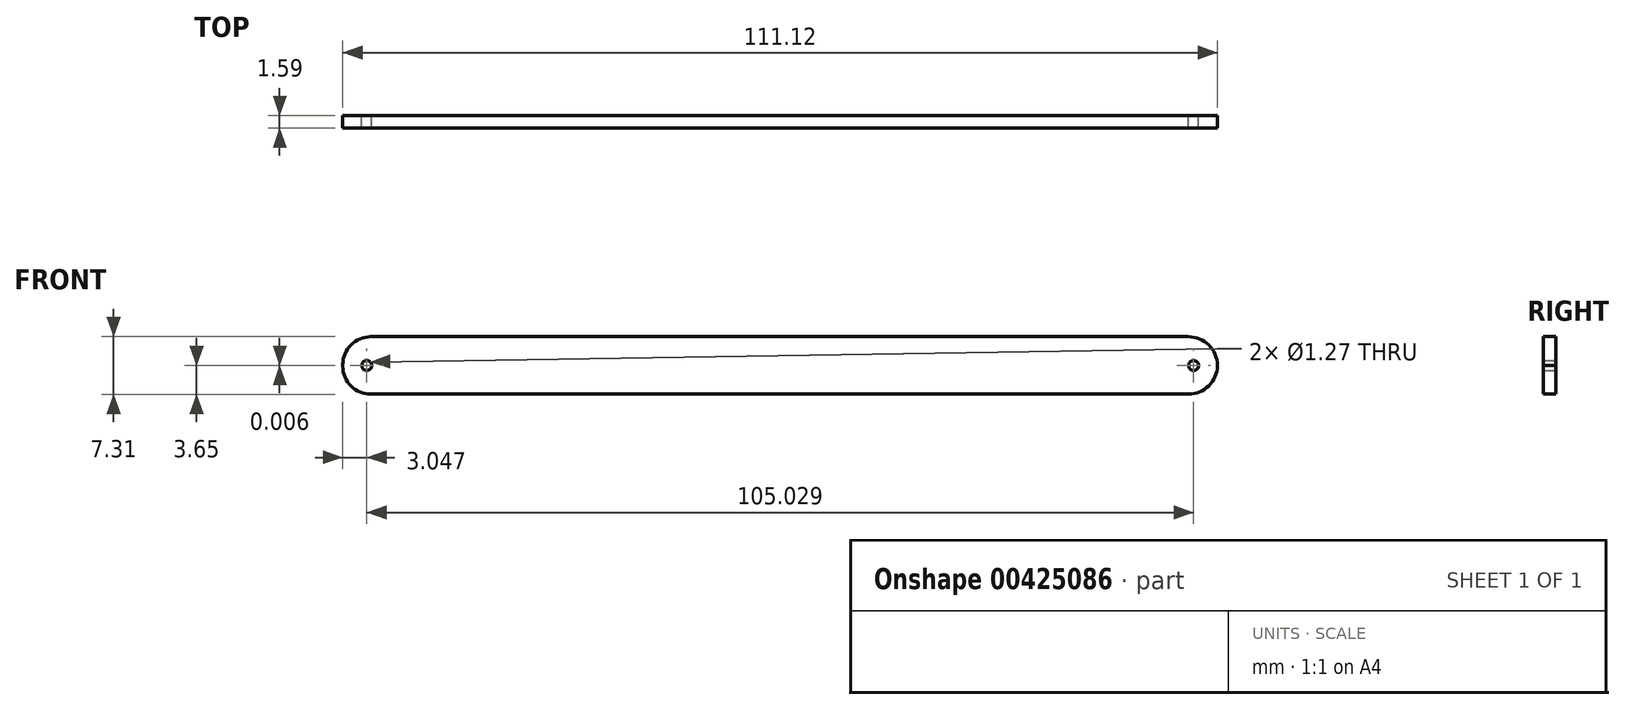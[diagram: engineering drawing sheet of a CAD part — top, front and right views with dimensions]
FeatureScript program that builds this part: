
annotation { "Feature Type Name" : "Feature", "Feature Type Description" : "" }
export const myFeature = defineFeature(function(context is Context, id is Id, definition is map)
    precondition{}
    {
        {
            var Q0;
            Q0=qCreatedBy(makeId("Front.planeOp"),FACE);
            var sketch = newSketch(context, id + "F0", { "sketchPlane" : qUnion([Q0])});
            skLineSegment(sketch, "E0.bottom", {"start": v(-46.8, 13.78) * mm, "end": v(64.33, 13.78) * mm});
            skLineSegment(sketch, "E0.top", {"start": v(-46.8, 6.47) * mm, "end": v(64.33, 6.47) * mm});
            skLineSegment(sketch, "E0.left", {"start": v(-46.8, 13.78) * mm, "end": v(-46.8, 6.47) * mm});
            skLineSegment(sketch, "E0.right", {"start": v(64.33, 13.78) * mm, "end": v(64.33, 6.47) * mm});
            skCircle(sketch, "E1", {"center": v(-43.74, 10.13) * mm, "radius": 0.64 * mm});
            skCircle(sketch, "E2", {"center": v(61.29, 10.12) * mm, "radius": 0.64 * mm});
            skSolve(sketch);
        }
        {
            var Q0;
            Q0 = qSketchRegion(id + "F0", true);
            extrude(context, id + "F1", {"entities" : qUnion([Q0]), "depth" : 1.59 * mm});
        }
        {
            var Q0;
            Q0=makeQuery(id+"F1.opExtrude","SWEPT_EDGE",EDGE,{"disambiguationData":[OSD([sQuery(id+"F0.wireOp",EDGE,"E0.bottom"),sQuery(id+"F0.wireOp",EDGE,"E0.left")])]});
            var Q1;
            Q1=makeQuery(id+"F1.opExtrude","SWEPT_EDGE",EDGE,{"disambiguationData":[OSD([sQuery(id+"F0.wireOp",EDGE,"E0.top"),sQuery(id+"F0.wireOp",EDGE,"E0.left")])]});
            fillet(context, id + "F2", {"entities" : qUnion([Q0, Q1]), "radius" : 3.56 * mm, "tangentPropagation" : true, "allowEdgeOverflow" : false});
        }
        {
            var Q0;
            Q0=makeQuery(id+"F1.opExtrude","SWEPT_EDGE",EDGE,{"disambiguationData":[OSD([sQuery(id+"F0.wireOp",EDGE,"E0.bottom"),sQuery(id+"F0.wireOp",EDGE,"E0.right")])]});
            var Q1;
            Q1=makeQuery(id+"F1.opExtrude","SWEPT_EDGE",EDGE,{"disambiguationData":[OSD([sQuery(id+"F0.wireOp",EDGE,"E0.top"),sQuery(id+"F0.wireOp",EDGE,"E0.right")])]});
            fillet(context, id + "F3", {"entities" : qUnion([Q0, Q1]), "radius" : 3.74 * mm, "tangentPropagation" : true, "allowEdgeOverflow" : false});
        }
    });
